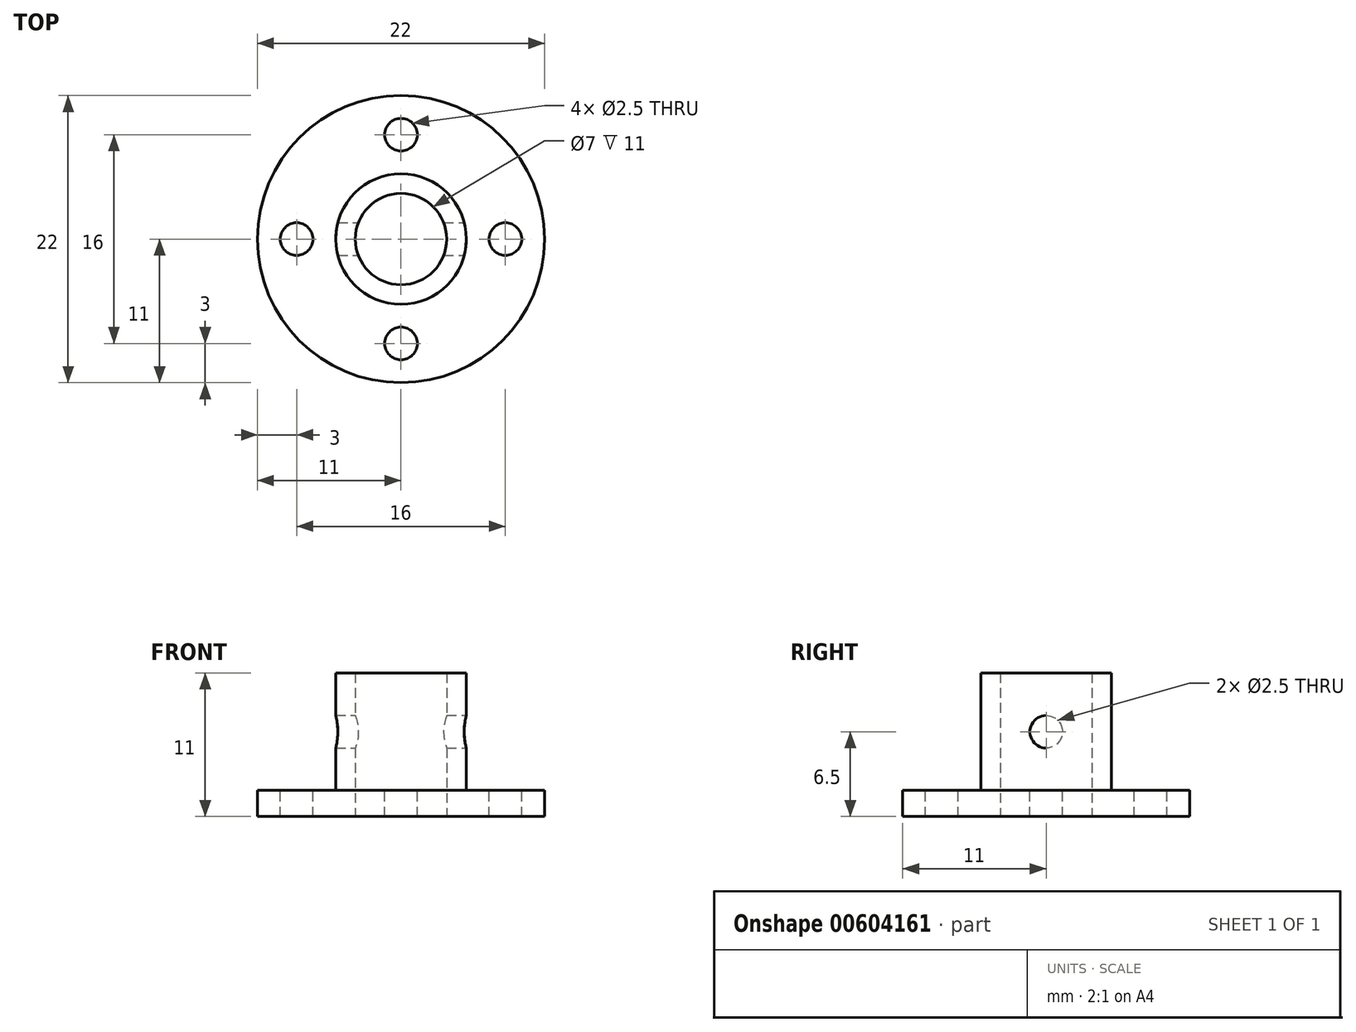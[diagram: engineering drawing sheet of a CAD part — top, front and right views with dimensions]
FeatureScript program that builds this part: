
annotation { "Feature Type Name" : "Feature", "Feature Type Description" : "" }
export const myFeature = defineFeature(function(context is Context, id is Id, definition is map)
    precondition{}
    {
        {
            var Q0;
            Q0=qCreatedBy(makeId("Top.planeOp"),FACE);
            var sketch = newSketch(context, id + "F0", { "sketchPlane" : qUnion([Q0])});
            skCircle(sketch, "E0", {"center": v(0, 0) * mm, "radius": 11 * mm});
            skSolve(sketch);
        }
        {
            var Q0;
            Q0 = qSketchRegion(id + "F0", true);
            extrude(context, id + "F1", {"entities" : qUnion([Q0]), "depth" : 2 * mm, "offsetDistance" : 25 * mm});
        }
        {
            var Q0;
            Q0=makeQuery(id+"F1.opExtrude","CAP_FACE",FACE,{"disambiguationData":[OSD([sQuery(id+"F0.wireOp",EDGE,"E0")])],"isStart":false});
            var sketch = newSketch(context, id + "F2", { "sketchPlane" : qUnion([Q0])});
            skCircle(sketch, "E1", {"center": v(0, 0) * mm, "radius": 5 * mm});
            skCircle(sketch, "E2", {"center": v(0, 0) * mm, "radius": 3.5 * mm});
            skSolve(sketch);
        }
        {
            var Q0;
            Q0=makeQuery(id+"F2.imprint","IMPRINT",FACE,{"disambiguationData":[TD([[makeQuery(id+"F2.imprint","IMPRINT",EDGE,{"derivedFrom":sQuery(id+"F2.wireOp",EDGE,"E1")}),1.0]])]});
            extrude(context, id + "F3", {"entities" : qUnion([Q0]), "operationType" : NewBodyOperationType.ADD, "depth" : 9 * mm, "offsetDistance" : 25 * mm});
        }
        {
            var Q0;
            Q0=makeQuery(id+"F3.boolean.opBoolean","SPLIT",FACE,{"disambiguationData":[TD([makeQuery(id+"F3.opExtrude","SWEPT_FACE",FACE,{"disambiguationData":[OSD([sQuery(id+"F2.wireOp",EDGE,"E2")])]})])],"derivedFrom":makeQuery(id+"F1.opExtrude","CAP_FACE",FACE,{"disambiguationData":[OSD([sQuery(id+"F0.wireOp",EDGE,"E0")])],"isStart":false})});
            var sketch = newSketch(context, id + "F4", { "sketchPlane" : qUnion([Q0])});
            skCircle(sketch, "E3", {"center": v(0, 0) * mm, "radius": 3.5 * mm});
            skSolve(sketch);
        }
        {
            var Q0;
            Q0 = qSketchRegion(id + "F4", true);
            var Q1;
            Q1=makeQuery(id+"F1.opExtrude","CAP_FACE",FACE,{"disambiguationData":[OSD([sQuery(id+"F0.wireOp",EDGE,"E0")])],"isStart":true});
            extrude(context, id + "F5", {"entities" : qUnion([Q0]), "operationType" : NewBodyOperationType.REMOVE, "endBound" : BoundingType.UP_TO_SURFACE, "oppositeDirection" : true, "depth" : 25 * mm, "endBoundEntityFace" : qUnion([Q1]), "offsetDistance" : 25 * mm});
        }
        {
            var Q0;
            {var subQ0=sQuery(id+"F0.wireOp",EDGE,"E0");Q0=makeQuery(id+"F3.boolean.opBoolean","SPLIT",FACE,{"disambiguationData":[TD([makeQuery(id+"F1.opExtrude","SWEPT_FACE",FACE,{"disambiguationData":[OSD([subQ0])]})])],"derivedFrom":makeQuery(id+"F1.opExtrude","CAP_FACE",FACE,{"disambiguationData":[OSD([subQ0])],"isStart":false})});}
            var sketch = newSketch(context, id + "F6", { "sketchPlane" : qUnion([Q0])});
            skCircle(sketch, "E4", {"center": v(0, 0) * mm, "radius": 8 * mm, "construction": true});
            skLineSegment(sketch, "E5", {"start": v(-8, 0) * mm, "end": v(8, 0) * mm, "construction": true});
            skLineSegment(sketch, "E6", {"start": v(0, 8) * mm, "end": v(0, -8) * mm, "construction": true});
            skSolve(sketch);
        }
        {
            var Q0;
            Q0=sQuery(id+"F6.wireOp",VERTEX,"E6.start");
            var Q1;
            Q1=sQuery(id+"F6.wireOp",VERTEX,"E5.end");
            var Q2;
            Q2=sQuery(id+"F6.wireOp",VERTEX,"E6.end");
            var Q3;
            Q3=sQuery(id+"F6.wireOp",VERTEX,"E5.start");
            var Q4;
            Q4=makeQuery(id+"F1.opExtrude","SWEPT_BODY",BODY,{"disambiguationData":[OSD([sQuery(id+"F0.wireOp",EDGE,"E0")])]});
            hole(context, id + "F7", {"style" : HoleStyle.SIMPLE, "endStyle" : HoleEndStyle.THROUGH, "standardTappedOrClearance" : lookupTablePath({ "standard" : "ISO", "engagement" : "75%", "pitch" : "0.5 mm", "size" : "M3", "type" : "Tapped" }), "standardBlindInLast" : lookupTablePath({ "standard" : "ISO", "engagement" : "75%", "pitch" : "0.5 mm", "size" : "M3", "type" : "Tapped" }), "holeDiameter" : 2.5 * mm, "majorDiameter" : 3 * mm, "showTappedDepth" : true, "isTappedThrough" : true, "tappedDepth" : 12 * mm, "tapClearance" : 3, "locations" : qUnion([Q0, Q1, Q2, Q3]), "scope" : qUnion([Q4])});
        }
        {
            var Q0;
            Q0=qCreatedBy(makeId("Right.planeOp"),FACE);
            cPlane(context, id + "F8", {"entities" : qUnion([Q0]), "cplaneType" : CPlaneType.OFFSET, "offset" : 5 * mm, "width" : 150 * mm, "height" : 150 * mm});
        }
        {
            var Q0;
            Q0=qCreatedBy(id+"F8.planeOp",FACE);
            var sketch = newSketch(context, id + "F9", { "sketchPlane" : qUnion([Q0])});
            skLineSegment(sketch, "E7", {"start": v(0, 0) * mm, "end": v(0, 11) * mm, "construction": true});
            skLineSegment(sketch, "E8", {"start": v(0, 11) * mm, "end": v(0, 6.5) * mm, "construction": true});
            skSolve(sketch);
        }
        {
            var Q0;
            Q0=sQuery(id+"F9.wireOp",VERTEX,"E8.end");
            var Q1;
            Q1=makeQuery(id+"F1.opExtrude","SWEPT_BODY",BODY,{"disambiguationData":[OSD([sQuery(id+"F0.wireOp",EDGE,"E0")])]});
            hole(context, id + "F10", {"style" : HoleStyle.SIMPLE, "endStyle" : HoleEndStyle.THROUGH, "standardTappedOrClearance" : lookupTablePath({ "standard" : "ISO", "engagement" : "75%", "pitch" : "0.5 mm", "size" : "M3", "type" : "Tapped" }), "standardBlindInLast" : lookupTablePath({ "standard" : "ISO", "engagement" : "75%", "pitch" : "0.5 mm", "size" : "M3", "type" : "Tapped" }), "holeDiameter" : 2.5 * mm, "majorDiameter" : 3 * mm, "showTappedDepth" : true, "isTappedThrough" : true, "tappedDepth" : 12 * mm, "tapClearance" : 3, "locations" : qUnion([Q0]), "scope" : qUnion([Q1])});
        }
    });
